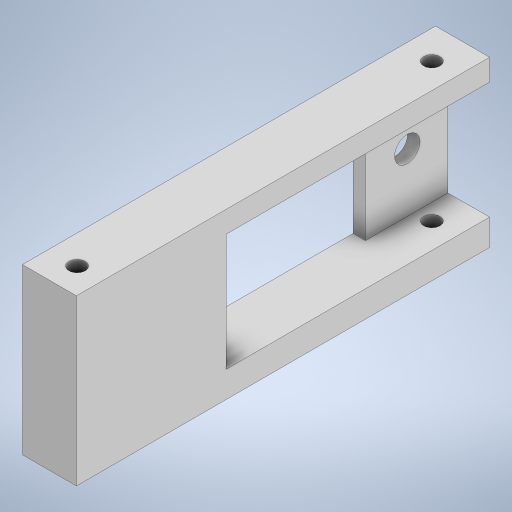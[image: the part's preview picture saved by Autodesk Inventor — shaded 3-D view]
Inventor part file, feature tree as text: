
AUTODESK INVENTOR PART (.ipt)
format: ipt  version: 2024.2 (Build 282272000, 272)  size: 219,648 bytes
history: native  units: mm
features: extrude x3, sketch x2, other x1
ambient origin geometry x8: Origin, YZ Plane, XZ Plane, XY Plane, X Axis, Y Axis, Z Axis, Center Point
bodies: Body1 (feature_tree)
feature tree (6):
  other  "Твердое тело1"
  extrude  "Выдавливание1"  Depth=43.073mm
  sketch  "Эскиз2"
  extrude  "Выдавливание2"  Depth=2.0mm
  extrude  "Выдавливание3"  Depth=2.0mm
  sketch  "Эскиз1"
